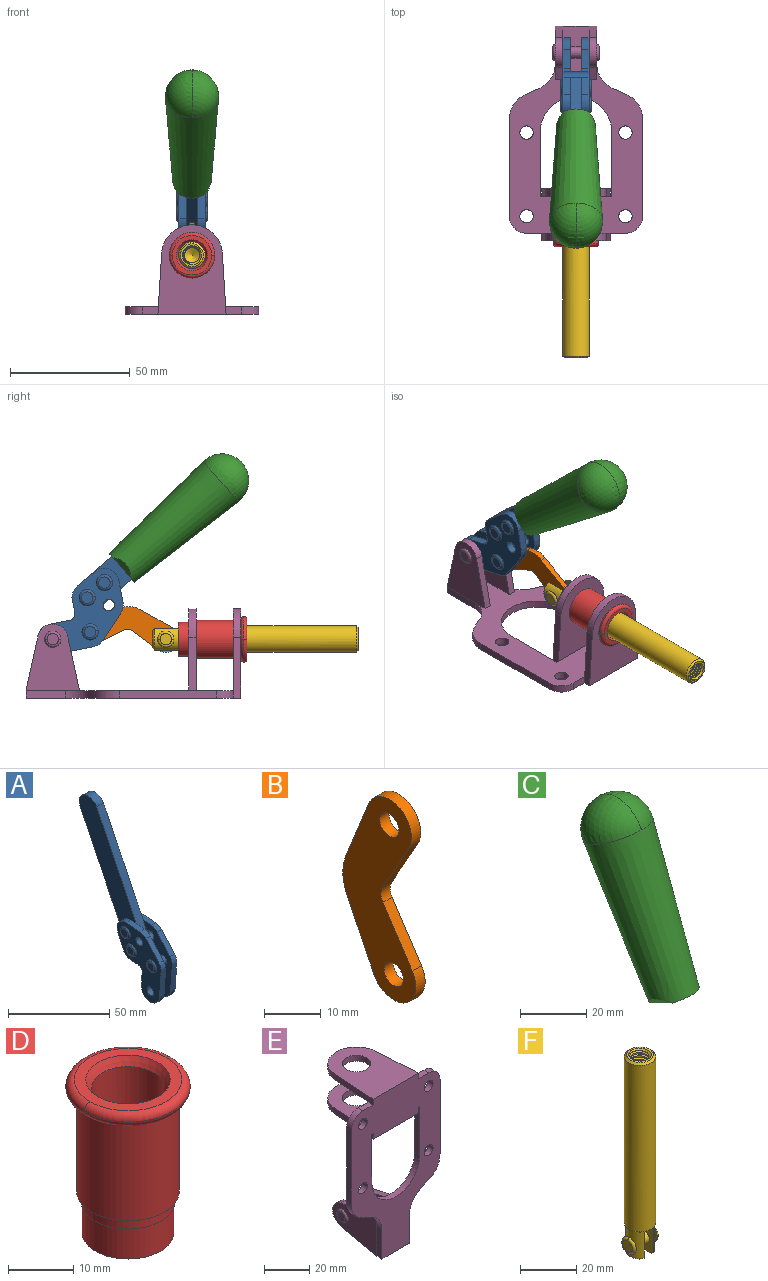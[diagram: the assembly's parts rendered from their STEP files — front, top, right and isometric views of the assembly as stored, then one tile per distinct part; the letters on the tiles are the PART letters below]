
ASSEMBLY  parts=6 mates=6
PART A: 59 faces, bbox 12.9x60.2x99.6 mm
  f0: torus R=2.39mm, axis (-1,0,0), area 14.9mm2, adj f20,f43,f51
  f1: torus R=2.39mm, axis (-1,0,0), area 14.9mm2, adj f19,f42,f51
  f2: torus R=2.39mm, axis (-1,0,0), area 14.9mm2, adj f18,f35,f51
  f3: torus R=2.39mm, axis (-1,0,0), area 14.9mm2, adj f14,f17,f23
  f4: torus R=2.39mm, axis (-1,0,0), area 14.9mm2, adj f13,f16,f23
  f5: torus R=2.39mm, axis (-1,0,0), area 14.9mm2, adj f12,f15,f23
  f6: cylinder r=2.39mm len=4.78mm, axis (1,0,0), area 46.5mm2, adj f48,f50,f51
  f7: cylinder r=2.39mm len=4.78mm, axis (1,0,0), area 46.5mm2, adj f50,f51
  f8: cylinder r=6.35mm len=12.68mm, axis (1,0,0), area 61.8mm2, adj f38,f39,f50,f51
  f9: cylinder r=2.39mm len=4.78mm, axis (-1,0,0), area 70.5mm2, adj f46,f50
  f10: cylinder r=2.39mm len=4.78mm, axis (-1,0,0), area 46.5mm2, adj f23,f45,f46
  f11: cylinder r=2.39mm len=4.78mm, axis (-1,0,0), area 46.5mm2, adj f23,f46
  f12: plane 4.78x4.78mm, normal (1,0,0), area 17.9mm2, adj f5,f15
  f13: plane 4.78x4.78mm, normal (1,0,0), area 17.9mm2, adj f4,f16
  f14: plane 4.78x4.78mm, normal (1,0,0), area 17.9mm2, adj f3,f17
  f15: torus R=2.39mm, axis (-1,0,0), area 14.9mm2, adj f5,f12,f23
  f16: torus R=2.39mm, axis (-1,0,0), area 14.9mm2, adj f4,f13,f23
  f17: torus R=2.39mm, axis (-1,0,0), area 14.9mm2, adj f3,f14,f23
  f18: plane 4.78x4.78mm, normal (-1,0,0), area 17.9mm2, adj f2,f35
  f19: plane 4.78x4.78mm, normal (-1,0,0), area 17.9mm2, adj f1,f42
  f20: plane 4.78x4.78mm, normal (-1,0,0), area 17.9mm2, adj f0,f43
  f21: plane 2.26x0.2mm, normal (1,0,0), area 0.2mm2, adj f31,f44
  f22: plane 2.26x0.2mm, normal (-1,0,0), area 0.2mm2, adj f41,f44
  f23: plane 39.37x30.77mm, normal (1,0,0), area 565.5mm2, adj f3,f4,f5,f10,f11,f15,f16,f17
  f24: cylinder r=6.1mm len=4.15mm, axis (-1,0,0), area 14.7mm2, adj f23,f25,f32,f46
  f25: plane 10.25x9.01mm, normal (0,-0.75,0.66), area 42.3mm2, adj f23,f24,f26,f46
  f26: cylinder r=6.35mm len=4.64mm, axis (-1,0,0), area 15.6mm2, adj f23,f25,f27,f46
  f27: plane 15.84x3.1mm, normal (0,-1,-0.07), area 49.2mm2, adj f23,f26,f28,f46
  f28: cylinder r=6.35mm len=12.68mm, axis (-1,0,0), area 61.8mm2, adj f23,f27,f29,f46
  f29: plane 8.11x3.1mm, normal (0,1,0.07), area 25.2mm2, adj f23,f28,f30,f46
  f30: cylinder r=3.05mm len=3.25mm, axis (-1,0,0), area 14.8mm2, adj f23,f29,f31,f46
  f31: plane 5.99x3.1mm, normal (0,0.07,-1), area 18.6mm2, adj f21,f23,f30,f44,f46
  f32: plane 9.5x3.1mm, normal (0,-0.07,1), area 29.5mm2, adj f23,f24,f33,f46,f47
  f33: cylinder r=6.1mm len=8.63mm, axis (-1,0,0), area 39.1mm2, adj f23,f32,f34,f47
  f34: plane 8.65x3.96mm, normal (0,0.91,-0.42), area 29.5mm2, adj f23,f33,f44,f47
  f35: torus R=2.39mm, axis (-1,0,0), area 14.9mm2, adj f2,f18,f51
  f36: plane 10.25x9.01mm, normal (0,-0.75,0.66), area 42.3mm2, adj f37,f49,f50,f51
  f37: cylinder r=6.35mm len=4.64mm, axis (1,0,0), area 15.6mm2, adj f36,f38,f50,f51
  f38: plane 15.84x3.1mm, normal (0,-1,-0.07), area 49.2mm2, adj f8,f37,f50,f51
  f39: plane 8.11x3.1mm, normal (0,1,0.07), area 25.2mm2, adj f8,f40,f50,f51
  f40: cylinder r=3.05mm len=3.25mm, axis (1,0,0), area 14.8mm2, adj f39,f41,f50,f51
  f41: plane 5.99x3.1mm, normal (0,0.07,-1), area 18.6mm2, adj f22,f40,f44,f50,f51
  f42: torus R=2.39mm, axis (-1,0,0), area 14.9mm2, adj f1,f19,f51
  f43: torus R=2.39mm, axis (-1,0,0), area 14.9mm2, adj f0,f20,f51
  f44: cylinder r=6.35mm len=12.12mm, axis (-1,0,0), area 128.9mm2, adj f21,f22,f23,f31,f34,f41,f46,f47
  f45: plane 2.65x1.35mm, normal (1,0,0), area 1mm2, adj f10,f55
  f46: plane 39.08x20.42mm, normal (-1,0,0), area 412.5mm2, adj f9,f10,f11,f24,f25,f26,f27,f28
  f47: plane 77.62x39.82mm, normal (1,0,0), area 850mm2, adj f32,f33,f34,f44,f53,f54,f55
  f48: plane 2.65x1.35mm, normal (-1,0,0), area 1mm2, adj f6,f55
  f49: cylinder r=6.1mm len=4.15mm, axis (1,0,0), area 14.7mm2, adj f36,f50,f51,f56
  f50: plane 39.08x20.42mm, normal (1,0,0), area 412.5mm2, adj f6,f7,f8,f9,f36,f37,f38,f39
  f51: plane 39.37x30.77mm, normal (-1,0,0), area 565.5mm2, adj f0,f1,f2,f6,f7,f8,f35,f36
  f52: plane 8.65x3.96mm, normal (0,0.91,-0.42), area 29.5mm2, adj f44,f51,f57,f58
  f53: plane 68.49x33.4mm, normal (0,0.9,-0.44), area 358.1mm2, adj f44,f47,f54,f58
  f54: cylinder r=6.35mm len=12.06mm, axis (1,0,0), area 93.7mm2, adj f47,f53,f55,f58
  f55: plane 68.49x33.4mm, normal (0,-0.9,0.44), area 358.1mm2, adj f44,f45,f46,f47,f48,f50,f54,f58
  f56: plane 9.5x3.1mm, normal (0,-0.07,1), area 29.5mm2, adj f49,f50,f51,f57,f58
  f57: cylinder r=6.1mm len=8.63mm, axis (1,0,0), area 39.1mm2, adj f51,f52,f56,f58
  f58: plane 77.62x39.82mm, normal (-1,0,0), area 850mm2, adj f44,f52,f53,f54,f55,f56,f57
PART B: 12 faces, bbox 2.3x18.2x42.8 mm
  f0: cylinder r=2.4mm len=4.8mm, axis (1,0,0), area 34.9mm2, adj f4,f11
  f1: cylinder r=10.41mm len=8.47mm, axis (1,0,0), area 20.2mm2, adj f4,f9,f10,f11
  f2: cylinder r=3.05mm len=3.16mm, axis (1,0,0), area 7.7mm2, adj f4,f6,f7,f11
  f3: cylinder r=2.4mm len=4.8mm, axis (1,0,0), area 34.9mm2, adj f4,f11
  f4: plane 42.81x18.23mm, normal (-1,0,0), area 414.1mm2, adj f0,f1,f2,f3,f5,f6,f7,f8
  f5: cylinder r=5.54mm len=10.67mm, axis (1,0,0), area 41.8mm2, adj f4,f6,f10,f11
  f6: plane 11.66x6.53mm, normal (0,-0.87,-0.49), area 30.9mm2, adj f2,f4,f5,f11
  f7: plane 11.17x7.33mm, normal (0,-0.84,0.55), area 30.9mm2, adj f2,f4,f8,f11
  f8: cylinder r=5.54mm len=10.51mm, axis (1,0,0), area 41.8mm2, adj f4,f7,f9,f11
  f9: plane 13.67x6.67mm, normal (0,0.9,-0.44), area 35.1mm2, adj f1,f4,f8,f11
  f10: plane 14.1x5.7mm, normal (0,0.93,0.37), area 35.1mm2, adj f1,f4,f5,f11
  f11: plane 42.81x18.23mm, normal (1,0,0), area 414.1mm2, adj f0,f1,f2,f3,f5,f6,f7,f8
PART C: 11 faces, bbox 22.3x42.6x64.5 mm
  f0: sphere r=11.13mm, area 411.4mm2, adj f1,f8
  f1: cone r=11.11mm half-angle=3.3deg, axis (0,0.44,0.9), area 3251.8mm2, adj f0,f7,f8,f9,f10
  f2: cylinder r=6.16mm len=11.7mm, axis (1,0,0), area 89.5mm2, adj f3,f4,f5,f6
  f3: plane 60.23x36.75mm, normal (-1,0,0), area 763.6mm2, adj f2,f4,f6,f10
  f4: plane 51.37x25.05mm, normal (0,0.9,-0.44), area 264.2mm2, adj f2,f3,f5,f10
  f5: plane 60.23x36.75mm, normal (1,0,0), area 763.6mm2, adj f2,f4,f6,f10
  f6: plane 51.37x25.05mm, normal (0,-0.9,0.44), area 264.2mm2, adj f2,f3,f5,f10
  f7: plane 9.95x5.95mm, normal (0.71,-0.31,-0.64), area 25.8mm2, adj f1,f10
  f8: sphere r=11.13mm, area 411.4mm2, adj f0,f1
  f9: plane 9.95x5.95mm, normal (-0.71,-0.31,-0.64), area 25.8mm2, adj f1,f10
  f10: plane 14.27x11.38mm, normal (0,-0.44,-0.9), area 106.7mm2, adj f1,f3,f4,f5,f6,f7,f9
PART D: 15 faces, bbox 20.6x20.6x28.7 mm
  f0: torus R=8.26mm, axis (0,0,1), area 56.8mm2, adj f1,f10,f12
  f1: torus R=8.26mm, axis (0,0,1), area 56.8mm2, adj f0,f6,f13
  f2: cylinder r=5.59mm len=25.91mm, axis (0,0,1), area 909.6mm2, adj f3,f4
  f3: cone r=6.86mm half-angle=45deg, axis (0,0,-1), area 70.2mm2, adj f2,f14
  f4: cone r=6.47mm half-angle=30deg, axis (0,0,1), area 66.7mm2, adj f2,f13
  f5: cylinder r=7.04mm len=14.07mm, axis (0,0,1), area 252.6mm2, adj f11,f14
  f6: torus R=8.26mm, axis (0,0,1), area 56.8mm2, adj f1,f12,f13
  f7: cylinder r=7.16mm len=14.33mm, axis (0,0,1), area 91.5mm2, adj f9,f11
  f8: cylinder r=7.86mm len=18.42mm, axis (0,0,1), area 909.6mm2, adj f9,f10
  f9: plane 15.72x15.72mm, normal (0,0,-1), area 33mm2, adj f7,f8
  f10: plane 16.51x16.51mm, normal (0,0,-1), area 19.9mm2, adj f0,f8,f12
  f11: plane 14.33x14.33mm, normal (0,0,-1), area 5.7mm2, adj f5,f7
  f12: torus R=8.26mm, axis (0,0,1), area 56.8mm2, adj f0,f6,f10
  f13: plane 16.51x16.51mm, normal (0,0,1), area 82.7mm2, adj f1,f4,f6
  f14: plane 14.07x14.07mm, normal (0,0,-1), area 7.8mm2, adj f3,f5
PART E: 55 faces, bbox 55.7x37.4x89.8 mm
  f0: torus R=2.41mm, axis (-1,0,0), area 15mm2, adj f11,f15,f25
  f1: torus R=2.41mm, axis (-1,0,0), area 15mm2, adj f10,f12,f22
  f2: cylinder r=2.78mm len=5.56mm, axis (0,-1,0), area 54.2mm2, adj f30,f54
  f3: cylinder r=14.99mm len=29.97mm, axis (0,-1,0), area 145.9mm2, adj f30,f49,f53,f54
  f4: cylinder r=2.78mm len=5.56mm, axis (0,-1,0), area 54.2mm2, adj f30,f54
  f5: cylinder r=2.78mm len=5.56mm, axis (0,-1,0), area 54.2mm2, adj f30,f54
  f6: cylinder r=2.78mm len=5.56mm, axis (0,-1,0), area 54.2mm2, adj f30,f54
  f7: cylinder r=6.35mm len=12.7mm, axis (0,0,1), area 123.6mm2, adj f27,f51
  f8: cylinder r=6.35mm len=12.7mm, axis (0,0,-1), area 124.7mm2, adj f21,f35
  f9: cylinder r=2.41mm len=11.18mm, axis (-1,0,0), area 169.4mm2, adj f16,f19
  f10: plane 4.83x4.83mm, normal (1,0,0), area 18.3mm2, adj f1,f12
  f11: plane 4.83x4.83mm, normal (-1,0,0), area 18.3mm2, adj f0,f15
  f12: torus R=2.41mm, axis (-1,0,0), area 15mm2, adj f1,f10,f22
  f13: cylinder r=6.35mm len=12.41mm, axis (1,0,0), area 53.4mm2, adj f18,f19,f22,f23
  f14: cylinder r=6.35mm len=12.41mm, axis (-1,0,0), area 53.4mm2, adj f16,f17,f24,f25
  f15: torus R=2.41mm, axis (-1,0,0), area 15mm2, adj f0,f11,f25
  f16: plane 27.86x22.35mm, normal (1,0,0), area 425.4mm2, adj f9,f14,f17,f24,f30
  f17: plane 22.86x4.97mm, normal (0,0.21,0.98), area 72.5mm2, adj f14,f16,f25,f30
  f18: plane 22.86x4.97mm, normal (0,0.21,0.98), area 72.5mm2, adj f13,f19,f22,f30
  f19: plane 27.86x22.35mm, normal (-1,0,0), area 425.4mm2, adj f9,f13,f18,f23,f30
  f20: cylinder r=12.7mm len=25.35mm, axis (0,0,-1), area 119.8mm2, adj f21,f34,f35,f36
  f21: plane 34.21x28.07mm, normal (0,0,-1), area 702.4mm2, adj f8,f20,f30,f34,f36
  f22: plane 27.96x22.45mm, normal (1,0,0), area 407.2mm2, adj f1,f12,f13,f18,f23,f30,f42,f43
  f23: plane 22.86x4.97mm, normal (0,0.21,-0.98), area 72.5mm2, adj f13,f19,f22,f44
  f24: plane 22.86x4.97mm, normal (0,0.21,-0.98), area 72.5mm2, adj f14,f16,f25,f44
  f25: plane 27.86x22.35mm, normal (-1,0,0), area 407.1mm2, adj f0,f14,f15,f17,f24,f30,f45,f46
  f26: plane 3.1x0.95mm, normal (0,0,-1), area 2.7mm2, adj f30,f49,f50,f54
  f27: plane 34.21x28.07mm, normal (0,0,1), area 702.4mm2, adj f7,f28,f30,f50,f52
  f28: cylinder r=12.7mm len=25.35mm, axis (0,0,1), area 118.8mm2, adj f27,f50,f51,f52
  f29: plane 3.1x0.95mm, normal (0,0,-1), area 2.7mm2, adj f30,f52,f53,f54
  f30: plane 86.54x55.63mm, normal (0,1,0), area 2362.9mm2, adj f2,f3,f4,f5,f6,f16,f17,f18
  f31: plane 40.56x3.1mm, normal (-1,0,0), area 125.7mm2, adj f30,f32,f48,f54
  f32: cylinder r=7.11mm len=7.11mm, axis (0,-1,0), area 34.6mm2, adj f30,f31,f33,f54
  f33: plane 6.67x3.1mm, normal (0,0,1), area 20.4mm2, adj f30,f32,f34,f54
  f34: plane 25.39x3.13mm, normal (-1,0.06,0), area 79.5mm2, adj f20,f21,f33,f35,f54
  f35: plane 37.31x28.45mm, normal (0,0,1), area 789.9mm2, adj f8,f20,f34,f36,f54
  f36: plane 25.39x3.13mm, normal (1,0.06,0), area 79.5mm2, adj f20,f21,f35,f37,f54
  f37: plane 6.67x3.1mm, normal (0,0,1), area 20.4mm2, adj f30,f36,f38,f54
  f38: cylinder r=7.11mm len=7.11mm, axis (0,-1,0), area 34.6mm2, adj f30,f37,f39,f54
  f39: plane 40.56x3.1mm, normal (1,0,0), area 125.7mm2, adj f30,f38,f40,f54
  f40: cylinder r=11.18mm len=10.16mm, axis (0,-1,0), area 39.5mm2, adj f30,f39,f41,f54
  f41: plane 6.09x3.1mm, normal (0.42,0,-0.91), area 20.8mm2, adj f30,f40,f42,f54
  f42: cylinder r=11.18mm len=9.41mm, axis (0,-1,0), area 37.2mm2, adj f22,f30,f41,f43,f54
  f43: plane 16.5x3.1mm, normal (1,0,0), area 51.1mm2, adj f22,f42,f44,f54
  f44: plane 17.37x3.1mm, normal (0,0,-1), area 53.8mm2, adj f23,f24,f30,f43,f45,f54
  f45: plane 16.5x3.1mm, normal (-1,0,0), area 51.1mm2, adj f25,f44,f46,f54
  f46: cylinder r=11.18mm len=9.41mm, axis (0,-1,0), area 37.2mm2, adj f25,f30,f45,f47,f54
  f47: plane 6.09x3.1mm, normal (-0.42,0,-0.91), area 20.8mm2, adj f30,f46,f48,f54
  f48: cylinder r=11.18mm len=10.16mm, axis (0,-1,0), area 39.5mm2, adj f30,f31,f47,f54
  f49: plane 26.54x3.1mm, normal (-1,0,0), area 82.3mm2, adj f3,f26,f30,f54
  f50: plane 25.39x3.1mm, normal (1,0.06,0), area 78.8mm2, adj f26,f27,f28,f51,f54
  f51: plane 37.31x28.45mm, normal (0,0,-1), area 789.9mm2, adj f7,f28,f50,f52,f54
  f52: plane 25.39x3.1mm, normal (-1,0.06,0), area 78.8mm2, adj f27,f28,f29,f51,f54
  f53: plane 26.54x3.1mm, normal (1,0,0), area 82.3mm2, adj f3,f29,f30,f54
  f54: plane 89.66x55.63mm, normal (0,-1,0), area 2678.5mm2, adj f2,f3,f4,f5,f6,f26,f29,f31
PART F: 48 faces, bbox 12.6x11.1x86.1 mm
  f0: torus R=2.41mm, axis (-1,0,0), area 15mm2, adj f30,f32,f34
  f1: torus R=2.41mm, axis (-1,0,0), area 15mm2, adj f29,f31,f33
  f2: cylinder r=5.54mm len=72.39mm, axis (0,0,1), area 2518.5mm2, adj f3,f4,f42,f43
  f3: cone r=5.54mm half-angle=45deg, axis (0,0,1), area 7.6mm2, adj f2,f5,f41
  f4: cone r=5.54mm half-angle=45deg, axis (0,0,-1), area 34.9mm2, adj f2,f39
  f5: cylinder r=5.08mm len=11.48mm, axis (0,0,1), area 108.3mm2, adj f3,f7,f8,f41
  f6: cylinder r=2.41mm len=4.83mm, axis (-1,0,0), area 71.2mm2, adj f40,f41
  f7: cylinder r=2.41mm len=4.83mm, axis (-1,0,0), area 7.6mm2, adj f5,f34
  f8: cone r=5.08mm half-angle=45deg, axis (0,0,1), area 10.6mm2, adj f5,f37,f41
  f9: cone r=3.98mm half-angle=45deg, axis (0,0,1), area 17.6mm2, adj f27,f39,f45,f46,f47
  f10: cylinder r=2.41mm len=4.83mm, axis (-1,0,0), area 7.6mm2, adj f33,f38
  f11: cylinder r=3.2mm len=6.4mm, axis (0,0,1), area 78.4mm2, adj f12,f28,f44,f45,f47
  f12: cylinder r=3.2mm len=6.4mm, axis (0,0,1), area 10.5mm2, adj f11,f13,f45,f47
  f13: cylinder r=3.2mm len=6.4mm, axis (0,0,1), area 10.5mm2, adj f12,f14,f45,f47
  f14: cylinder r=3.2mm len=6.4mm, axis (0,0,1), area 10.5mm2, adj f13,f15,f45,f47
  f15: cylinder r=3.2mm len=6.4mm, axis (0,0,1), area 10.5mm2, adj f14,f16,f45,f47
  f16: cylinder r=3.2mm len=6.4mm, axis (0,0,1), area 10.5mm2, adj f15,f17,f45,f47
  f17: cylinder r=3.2mm len=6.4mm, axis (0,0,1), area 10.5mm2, adj f16,f18,f45,f47
  f18: cylinder r=3.2mm len=6.4mm, axis (0,0,1), area 10.5mm2, adj f17,f19,f45,f47
  f19: cylinder r=3.2mm len=6.4mm, axis (0,0,1), area 10.5mm2, adj f18,f20,f45,f47
  f20: cylinder r=3.2mm len=6.4mm, axis (0,0,1), area 10.5mm2, adj f19,f21,f45,f47
  f21: cylinder r=3.2mm len=6.4mm, axis (0,0,1), area 10.5mm2, adj f20,f22,f45,f47
  f22: cylinder r=3.2mm len=6.4mm, axis (0,0,1), area 10.5mm2, adj f21,f23,f45,f47
  f23: cylinder r=3.2mm len=6.4mm, axis (0,0,1), area 10.5mm2, adj f22,f24,f45,f47
  f24: cylinder r=3.2mm len=6.4mm, axis (0,0,1), area 10.5mm2, adj f23,f25,f45,f47
  f25: cylinder r=3.2mm len=6.4mm, axis (0,0,1), area 10.5mm2, adj f24,f26,f45,f47
  f26: cylinder r=3.2mm len=6.4mm, axis (0,0,1), area 10.5mm2, adj f25,f27,f45,f47
  f27: cylinder r=3.2mm len=6.4mm, axis (0,0,1), area 7.4mm2, adj f9,f26,f45,f47
  f28: cone r=3.2mm half-angle=60deg, axis (0,0,1), area 37.2mm2, adj f11
  f29: plane 4.83x4.83mm, normal (-1,0,0), area 18.3mm2, adj f1,f31
  f30: plane 4.83x4.83mm, normal (1,0,0), area 18.3mm2, adj f0,f32
  f31: torus R=2.41mm, axis (-1,0,0), area 15mm2, adj f1,f29,f33
  f32: torus R=2.41mm, axis (-1,0,0), area 15mm2, adj f0,f30,f34
  f33: plane 6.83x6.83mm, normal (1,0,0), area 18.3mm2, adj f1,f10,f31
  f34: plane 6.83x6.83mm, normal (-1,0,0), area 18.3mm2, adj f0,f7,f32
  f35: cone r=5.08mm half-angle=45deg, axis (0,0,1), area 10.6mm2, adj f36,f38,f40
  f36: plane 7.25x1.97mm, normal (0,0,-1), area 10mm2, adj f35,f40
  f37: plane 7.25x1.97mm, normal (0,0,-1), area 10mm2, adj f8,f41
  f38: cylinder r=5.08mm len=11.48mm, axis (0,0,1), area 108.3mm2, adj f10,f35,f40,f42
  f39: plane 9.55x9.55mm, normal (0,0,1), area 22mm2, adj f4,f9
  f40: plane 12.76x10.09mm, normal (1,0,0), area 95.7mm2, adj f6,f35,f36,f38,f42,f43
  f41: plane 12.76x10.09mm, normal (-1,0,0), area 95.7mm2, adj f3,f5,f6,f8,f37,f43
  f42: cone r=5.54mm half-angle=45deg, axis (0,0,1), area 7.6mm2, adj f2,f38,f40
  f43: plane 11.07x4.7mm, normal (0,0,-1), area 50.4mm2, adj f2,f40,f41
  f44: plane 0.89x0.62mm, normal (-1,0,0), area 0.3mm2, adj f11,f45,f46,f47
  f45: bspline ~24.8x7.63mm, area 266.6mm2, adj f9,f11,f12,f13,f14,f15,f16,f17
  f46: bspline ~24.87x7.63mm, area 73.6mm2, adj f9,f44,f45,f47
  f47: bspline ~24.98x7.63mm, area 272.5mm2, adj f9,f11,f12,f13,f14,f15,f16,f17
PLACE A rot(axis=(1,0,0),75deg) t=(0,-5.28,9.14)mm
PLACE B rot(axis=(1,0,0),97.5deg) t=(0,3.45,2.22)mm
PLACE C rot(axis=(1,0,0),75deg) t=(0,-5.28,9.14)mm
PLACE D rot(axis=(1,0,0),90deg) t=(0,0,0)mm
PLACE E rot(axis=(1,0,0),90deg) t=(0,0,0)mm fixed
PLACE F rot(axis=(1,0,0),90deg) t=(0,0.38,0)mm
MATE revolute B.f3 <-> A.f4  axis (1,0,0) through (0,16.51,27.64)mm
MATE fastened E.f7 <-> D.f0  axis (0,-1,0) through (0,-46.39,24.61)mm
MATE fastened C.f2 <-> A.f54  axis (1,0,0) through (0,-39.8,91.94)mm
MATE revolute A.f7 <-> E.f0  axis (1,0,0) through (0,32.09,24.61)mm
MATE cylindrical F.f2 <-> E.f7  axis (0,-1,0) through (0,-58.4,24.61)mm
MATE revolute B.f5 <-> F.f6  axis (1,0,0) through (0,-15.1,24.61)mm
